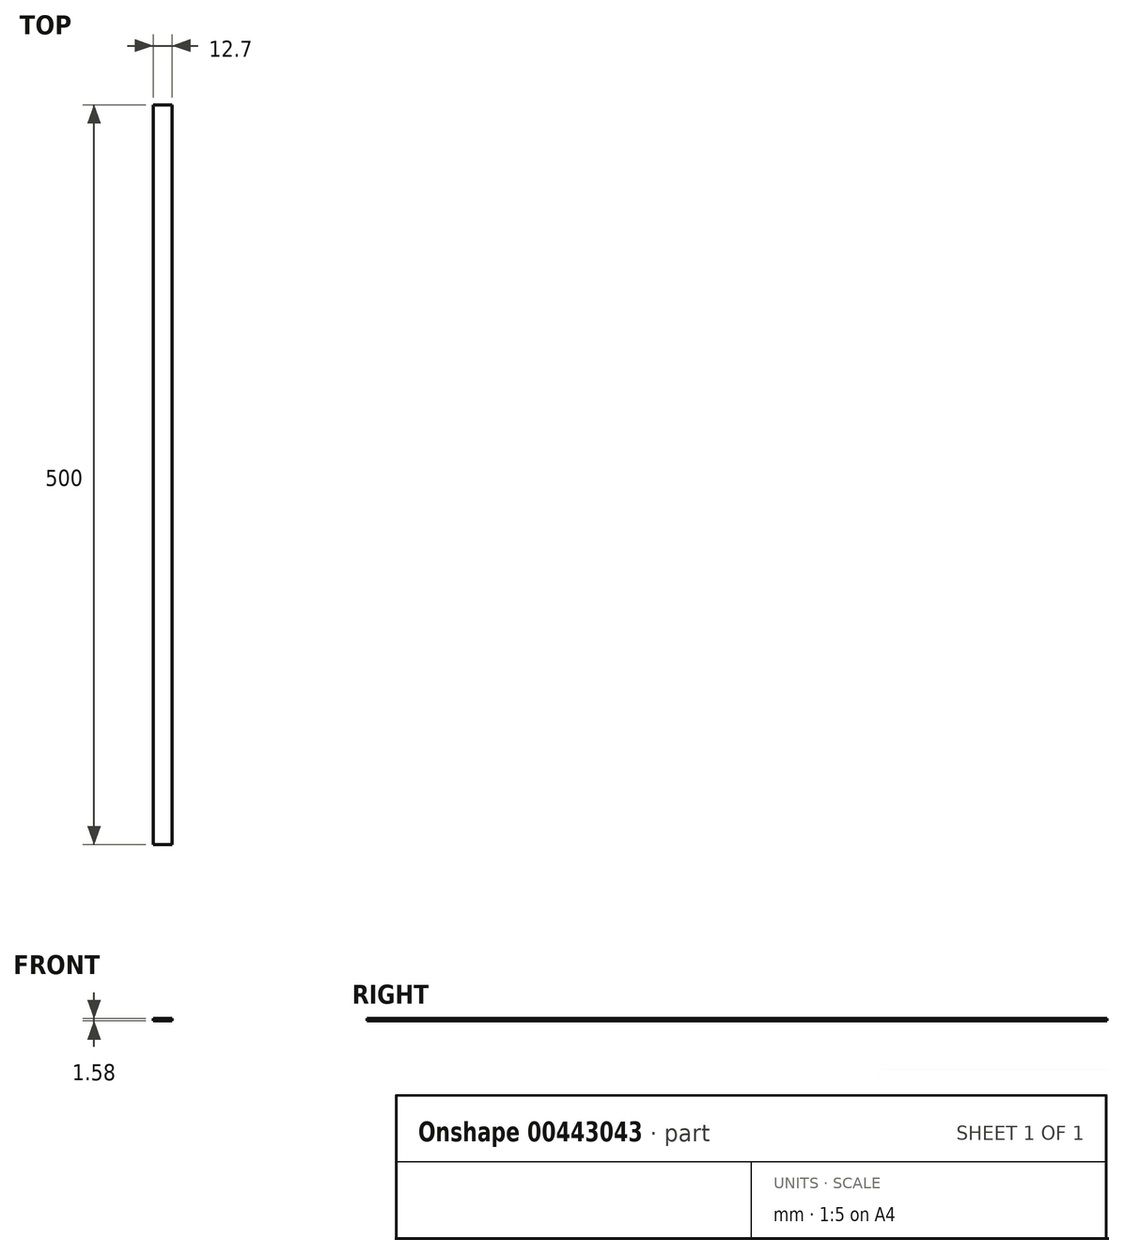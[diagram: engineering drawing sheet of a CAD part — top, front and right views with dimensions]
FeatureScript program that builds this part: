
annotation { "Feature Type Name" : "Feature", "Feature Type Description" : "" }
export const myFeature = defineFeature(function(context is Context, id is Id, definition is map)
    precondition{}
    {
        {
            var Q0;
            Q0=qCreatedBy(makeId("Front.planeOp"),FACE);
            var sketch = newSketch(context, id + "F0", { "sketchPlane" : qUnion([Q0])});
            skLineSegment(sketch, "E0.bottom", {"start": v(6.35, -0.8) * mm, "end": v(-6.35, -0.8) * mm});
            skLineSegment(sketch, "E0.top", {"start": v(6.35, 0.8) * mm, "end": v(-6.35, 0.8) * mm});
            skLineSegment(sketch, "E0.left", {"start": v(6.35, -0.8) * mm, "end": v(6.35, 0.8) * mm});
            skLineSegment(sketch, "E0.right", {"start": v(-6.35, -0.8) * mm, "end": v(-6.35, 0.8) * mm});
            skPoint(sketch, "E0.middle", {"position": v(0, 0) * mm});
            skSolve(sketch);
        }
        {
            var Q0;
            Q0=makeQuery(id+"F0.imprint","IMPRINT",FACE,{"disambiguationData":[TD([[makeQuery(id+"F0.imprint","IMPRINT",EDGE,{"derivedFrom":sQuery(id+"F0.wireOp",EDGE,"E0.bottom")}),-1.0]])]});
            extrude(context, id + "F1", {"entities" : qUnion([Q0]), "endBound" : BoundingType.SYMMETRIC, "depth" : 500 * mm});
        }
    });
